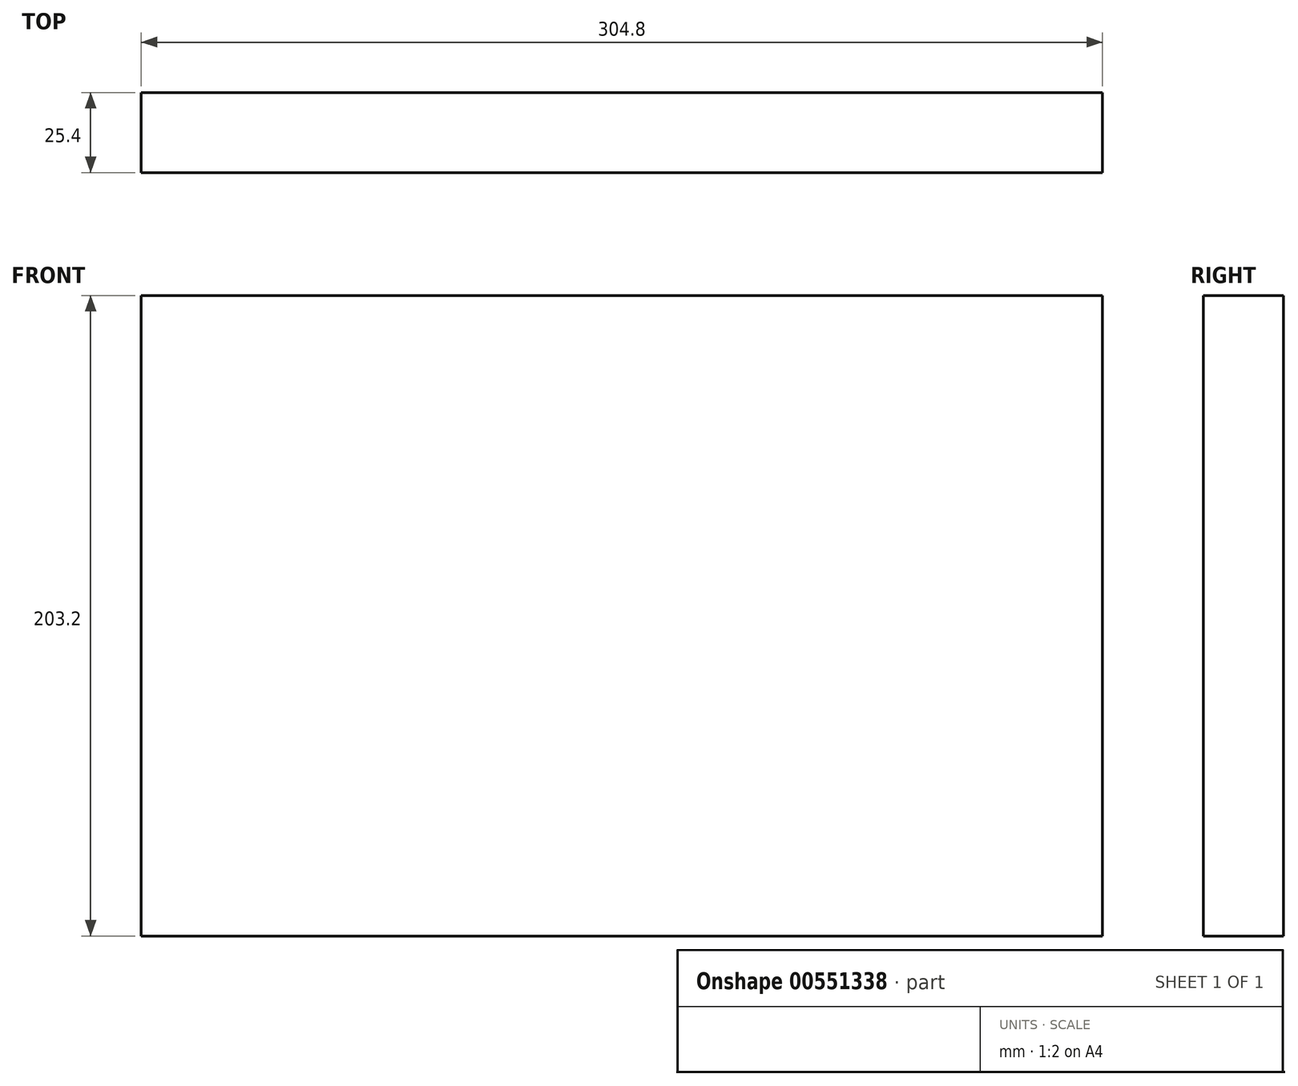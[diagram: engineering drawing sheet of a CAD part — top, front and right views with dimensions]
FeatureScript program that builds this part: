
annotation { "Feature Type Name" : "Feature", "Feature Type Description" : "" }
export const myFeature = defineFeature(function(context is Context, id is Id, definition is map)
    precondition{}
    {
        {
            var Q0;
            Q0=qCreatedBy(makeId("Front.planeOp"),FACE);
            var sketch = newSketch(context, id + "F0", { "sketchPlane" : qUnion([Q0])});
            skLineSegment(sketch, "E0.bottom", {"start": v(-112.99, 105.77) * mm, "end": v(191.81, 105.77) * mm});
            skLineSegment(sketch, "E0.top", {"start": v(-112.99, -97.43) * mm, "end": v(191.81, -97.43) * mm});
            skLineSegment(sketch, "E0.left", {"start": v(-112.99, 105.77) * mm, "end": v(-112.99, -97.43) * mm});
            skLineSegment(sketch, "E0.right", {"start": v(191.81, 105.77) * mm, "end": v(191.81, -97.43) * mm});
            skSolve(sketch);
        }
        {
            var Q0;
            Q0=makeQuery(id+"F0.imprint","IMPRINT",FACE,{"disambiguationData":[TD([[makeQuery(id+"F0.imprint","IMPRINT",EDGE,{"derivedFrom":sQuery(id+"F0.wireOp",EDGE,"E0.bottom")}),-1.0]])]});
            extrude(context, id + "F1", {"entities" : qUnion([Q0]), "depth" : 25.4 * mm, "offsetDistance" : 25.4 * mm});
        }
    });
